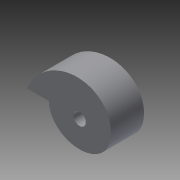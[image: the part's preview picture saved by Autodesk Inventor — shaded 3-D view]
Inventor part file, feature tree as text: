
AUTODESK INVENTOR PART (.ipt)
format: ipt  version: 2014 (Build 180170000, 170)  size: 98,816 bytes
history: native  units: in
note: dims shown in document units (in); Inventor stores cm internally (conversion verified against a paired STEP export)
features: extrude x1, sketch x1
ambient origin geometry x8: Origin, YZ Plane, XZ Plane, XY Plane, X Axis, Y Axis, Z Axis, Center Point
bodies: Solid1 (feature_tree)
feature tree (2):
  extrude  "Extrusion1"  Depth=0.664in
  sketch  "Sketch1"  dims[d18=1.59in d19=0.664in d29=1.6164in d30=1.406in d31=0.9869in d32=1.4075in d33=1.1558in d43=0.8251in d50=0.375in d51=1.0in d52=0.0in d60=0.926in d61=0.7976in d62=0.7134in d63=0.7293in]
